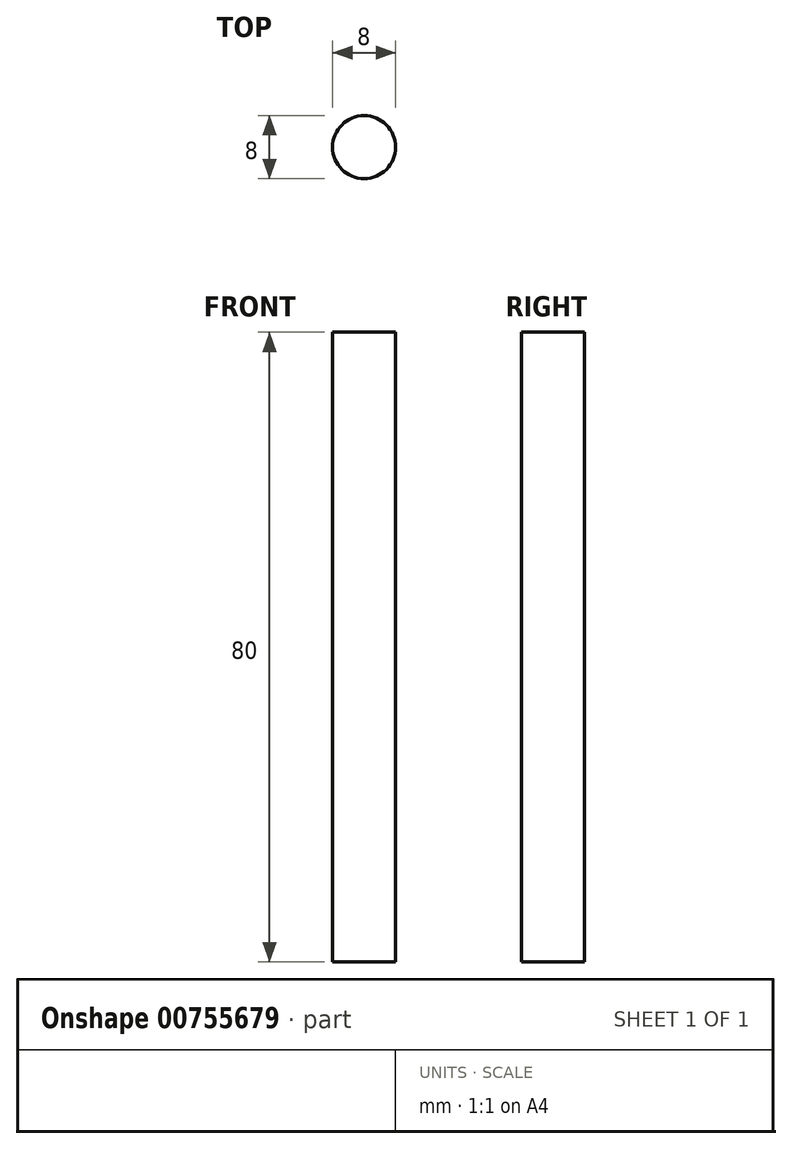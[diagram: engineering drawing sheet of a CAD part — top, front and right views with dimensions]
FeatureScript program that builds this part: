
annotation { "Feature Type Name" : "Feature", "Feature Type Description" : "" }
export const myFeature = defineFeature(function(context is Context, id is Id, definition is map)
    precondition{}
    {
        {
            var Q0;
            Q0=qCreatedBy(makeId("Top.planeOp"),FACE);
            var sketch = newSketch(context, id + "F0", { "sketchPlane" : qUnion([Q0])});
            skCircle(sketch, "E0", {"center": v(0, 0) * mm, "radius": 4 * mm});
            skSolve(sketch);
        }
        {
            var Q0;
            Q0=qSketchRegion(id+"F0",true);
            extrude(context, id + "F1", {"entities" : qUnion([Q0]), "depth" : 80 * mm, "offsetDistance" : 25 * mm});
        }
    });
